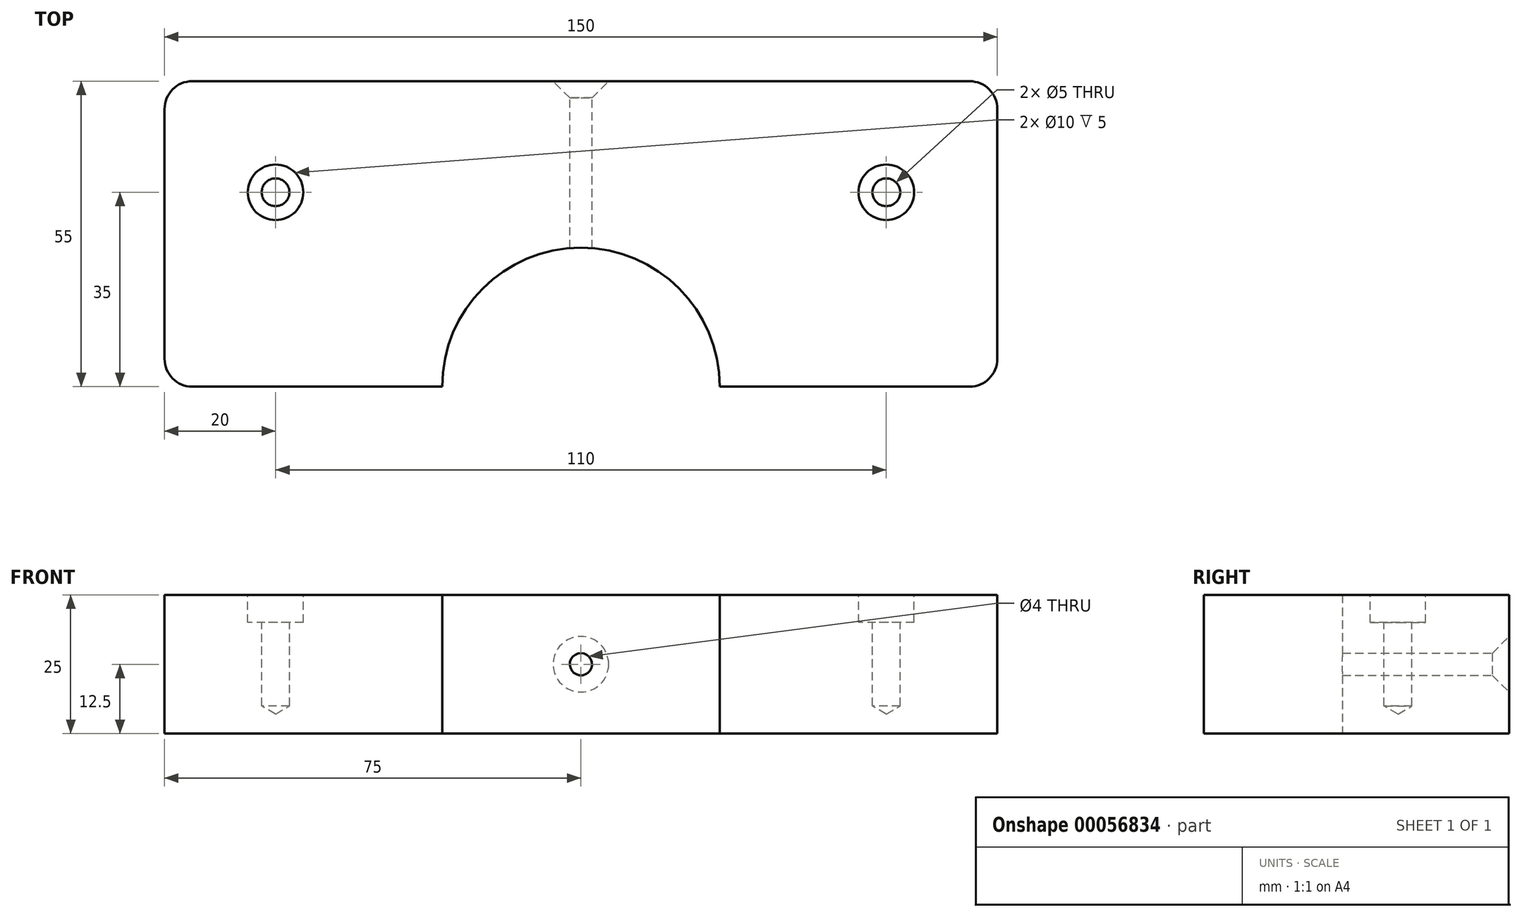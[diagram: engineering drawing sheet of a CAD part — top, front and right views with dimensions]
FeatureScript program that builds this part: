
annotation { "Feature Type Name" : "Feature", "Feature Type Description" : "" }
export const myFeature = defineFeature(function(context is Context, id is Id, definition is map)
    precondition{}
    {
        {
            var Q0;
            Q0=qCreatedBy(makeId("Top.planeOp"),FACE);
            var sketch = newSketch(context, id + "F0", { "sketchPlane" : qUnion([Q0])});
            skLineSegment(sketch, "E0.bottom", {"start": v(-75, 27.5) * mm, "end": v(75, 27.5) * mm});
            skLineSegment(sketch, "E0.top", {"start": v(-75, -27.5) * mm, "end": v(-25, -27.5) * mm});
            skLineSegment(sketch, "E0.left", {"start": v(-75, 27.5) * mm, "end": v(-75, -27.5) * mm});
            skLineSegment(sketch, "E0.right", {"start": v(75, 27.5) * mm, "end": v(75, -27.5) * mm});
            skArc(sketch, "E1", {"start": v(25, -27.5) * mm, "mid": v(0, -2.5) * mm, "end": v(-25, -27.5) * mm});
            skLineSegment(sketch, "E2.trimOffspring", {"start": v(25, -27.5) * mm, "end": v(75, -27.5) * mm});
            skSolve(sketch);
        }
        {
            var Q0;
            Q0=makeQuery(id+"F0.imprint","IMPRINT",FACE,{"disambiguationData":[TD([[makeQuery(id+"F0.imprint","IMPRINT",EDGE,{"derivedFrom":sQuery(id+"F0.wireOp",EDGE,"E0.bottom")}),-1.0]])]});
            extrude(context, id + "F1", {"entities" : qUnion([Q0]), "endBound" : BoundingType.SYMMETRIC, "depth" : 25 * mm});
        }
        {
            var Q0;
            Q0=makeQuery(id+"F1.opExtrude","SWEPT_EDGE",EDGE,{"disambiguationData":[OSD([sQuery(id+"F0.wireOp",EDGE,"E0.bottom"),sQuery(id+"F0.wireOp",EDGE,"E0.right")])]});
            var Q1;
            Q1=makeQuery(id+"F1.opExtrude","SWEPT_EDGE",EDGE,{"disambiguationData":[OSD([sQuery(id+"F0.wireOp",EDGE,"E0.bottom"),sQuery(id+"F0.wireOp",EDGE,"E0.left")])]});
            var Q2;
            Q2=makeQuery(id+"F1.opExtrude","SWEPT_EDGE",EDGE,{"disambiguationData":[OSD([sQuery(id+"F0.wireOp",EDGE,"E0.top"),sQuery(id+"F0.wireOp",EDGE,"E0.left")])]});
            var Q3;
            Q3=makeQuery(id+"F1.opExtrude","SWEPT_EDGE",EDGE,{"disambiguationData":[OSD([sQuery(id+"F0.wireOp",EDGE,"E0.right"),sQuery(id+"F0.wireOp",EDGE,"E2.trimOffspring")])]});
            fillet(context, id + "F2", {"entities" : qUnion([Q0, Q1, Q2, Q3]), "radius" : 5 * mm, "tangentPropagation" : true, "allowEdgeOverflow" : false});
        }
        {
            var Q0;
            Q0=makeQuery(id+"F1.opExtrude","CAP_FACE",FACE,{"disambiguationData":[OSD([sQuery(id+"F0.wireOp",EDGE,"E0.bottom"),sQuery(id+"F0.wireOp",EDGE,"E0.top"),sQuery(id+"F0.wireOp",EDGE,"E0.left"),sQuery(id+"F0.wireOp",EDGE,"E0.right"),sQuery(id+"F0.wireOp",EDGE,"E1"),sQuery(id+"F0.wireOp",EDGE,"E2.trimOffspring")])],"isStart":false});
            var sketch = newSketch(context, id + "F3", { "sketchPlane" : qUnion([Q0])});
            skPoint(sketch, "E3", {"position": v(-55, 7.5) * mm});
            skPoint(sketch, "E4.MirrorP", {"position": v(55, 7.5) * mm});
            skSolve(sketch);
        }
        {
            var Q0;
            Q0=sQuery(id+"F3.wireOp",VERTEX,"E3");
            var Q1;
            Q1=sQuery(id+"F3.wireOp",VERTEX,"E4.MirrorP");
            var Q2;
            Q2=makeQuery(id+"F1.opExtrude","SWEPT_BODY",BODY,{"disambiguationData":[OSD([sQuery(id+"F0.wireOp",EDGE,"E0.bottom"),sQuery(id+"F0.wireOp",EDGE,"E0.top"),sQuery(id+"F0.wireOp",EDGE,"E0.left"),sQuery(id+"F0.wireOp",EDGE,"E0.right"),sQuery(id+"F0.wireOp",EDGE,"E1"),sQuery(id+"F0.wireOp",EDGE,"E2.trimOffspring")])]});
            hole(context, id + "F4", {"style" : HoleStyle.C_BORE, "holeDiameter" : 5 * mm, "cBoreDiameter" : 10 * mm, "cBoreDepth" : 5 * mm, "endStyle" : HoleEndStyle.BLIND, "holeDepth" : 20 * mm, "locations" : qUnion([Q0, Q1]), "scope" : qUnion([Q2])});
        }
        {
            var Q0;
            Q0=makeQuery(id+"F1.opExtrude","SWEPT_FACE",FACE,{"disambiguationData":[OSD([sQuery(id+"F0.wireOp",EDGE,"E0.bottom")])]});
            var sketch = newSketch(context, id + "F5", { "sketchPlane" : qUnion([Q0])});
            skPoint(sketch, "E5", {"position": v(0, 0) * mm});
            skSolve(sketch);
        }
        {
            var Q0;
            Q0=sQuery(id+"F5.wireOp",VERTEX,"E5");
            var Q1;
            Q1=makeQuery(id+"F1.opExtrude","SWEPT_BODY",BODY,{"disambiguationData":[OSD([sQuery(id+"F0.wireOp",EDGE,"E0.bottom"),sQuery(id+"F0.wireOp",EDGE,"E0.top"),sQuery(id+"F0.wireOp",EDGE,"E0.left"),sQuery(id+"F0.wireOp",EDGE,"E0.right"),sQuery(id+"F0.wireOp",EDGE,"E1"),sQuery(id+"F0.wireOp",EDGE,"E2.trimOffspring")])]});
            hole(context, id + "F6", {"style" : HoleStyle.C_SINK, "holeDiameter" : 4 * mm, "cSinkDiameter" : 10 * mm, "endStyle" : HoleEndStyle.THROUGH, "locations" : qUnion([Q0]), "scope" : qUnion([Q1]), "cSinkAngle" : 90 * degree});
        }
    });
